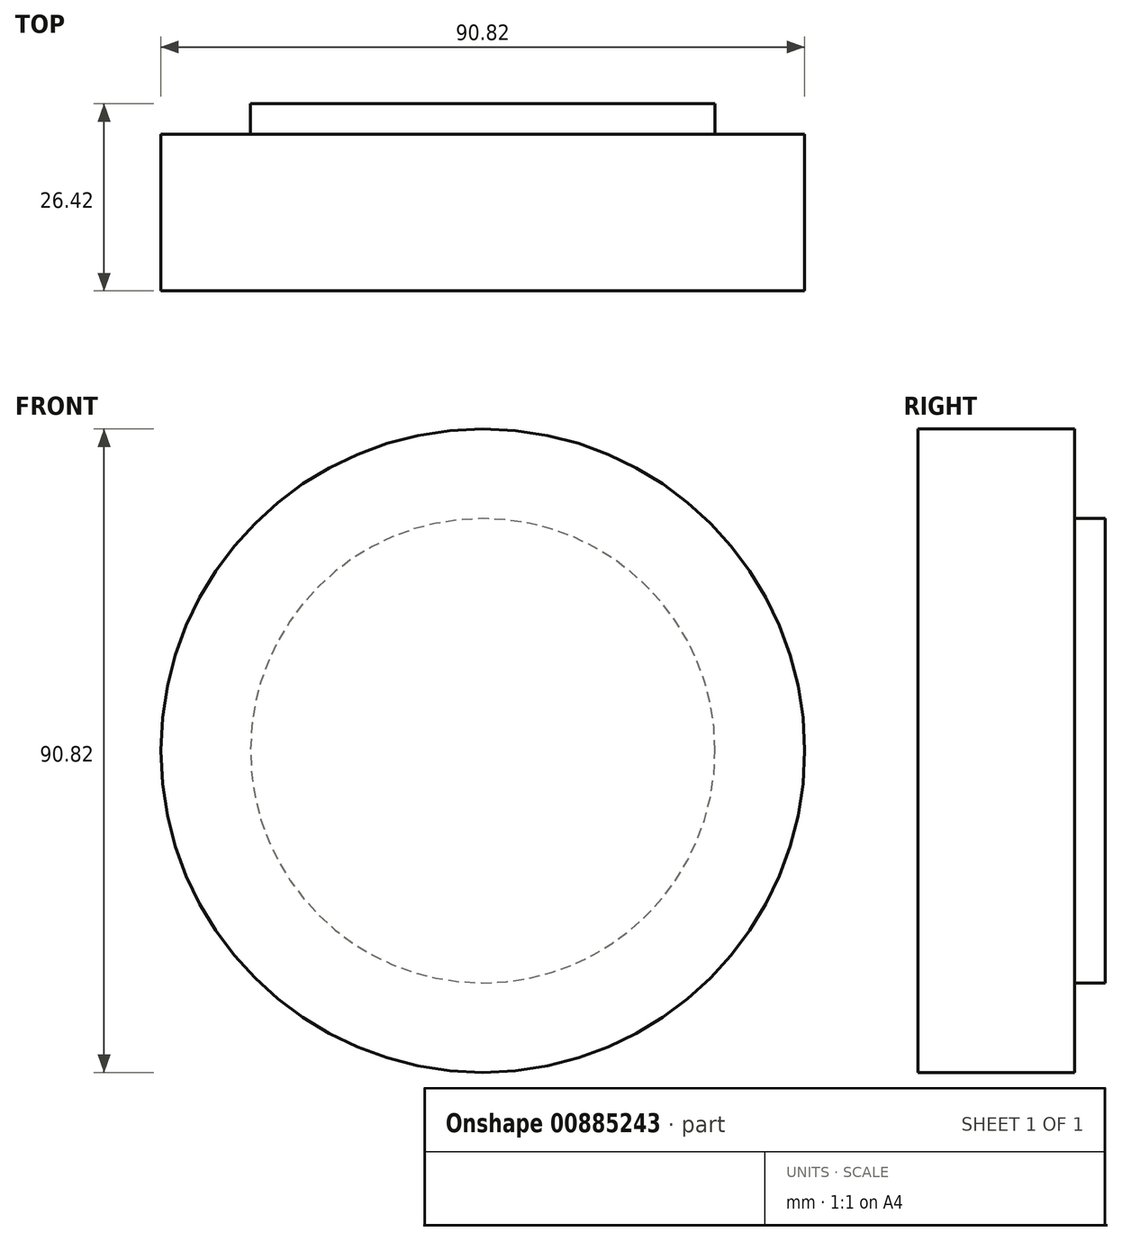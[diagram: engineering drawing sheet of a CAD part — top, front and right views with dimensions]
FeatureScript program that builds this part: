
annotation { "Feature Type Name" : "Feature", "Feature Type Description" : "" }
export const myFeature = defineFeature(function(context is Context, id is Id, definition is map)
    precondition{}
    {
        {
            var Q0;
            Q0=qCreatedBy(makeId("Front.planeOp"),FACE);
            var sketch = newSketch(context, id + "F0", { "sketchPlane" : qUnion([Q0])});
            skCircle(sketch, "E0", {"center": v(0, 0) * mm, "radius": 45.41 * mm});
            skCircle(sketch, "E1", {"center": v(0, 0) * mm, "radius": 32.77 * mm});
            skSolve(sketch);
        }
        {
            var Q0;
            Q0=makeQuery(id+"F0.imprint","IMPRINT",FACE,{"disambiguationData":[TD([[makeQuery(id+"F0.imprint","IMPRINT",EDGE,{"derivedFrom":sQuery(id+"F0.wireOp",EDGE,"E1")}),1.0]])]});
            extrude(context, id + "F1", {"entities" : qUnion([Q0]), "oppositeDirection" : true, "depth" : 4.32 * mm, "offsetDistance" : 25.4 * mm});
        }
        {
            var Q0;
            Q0 = qSketchRegion(id + "F0", true);
            var Q1;
            Q1=makeQuery(id+"F1.opExtrude","CAP_FACE",FACE,{"disambiguationData":[OSD([sQuery(id+"F0.wireOp",EDGE,"E1")])],"isStart":false});
            var Q2;
            Q2=makeQuery(id+"F1.opExtrude","CAP_FACE",FACE,{"disambiguationData":[OSD([sQuery(id+"F0.wireOp",EDGE,"E1")])],"isStart":true});
            extrude(context, id + "F2", {"entities" : qUnion([Q0, Q1, Q2]), "operationType" : NewBodyOperationType.ADD, "oppositeDirection" : true, "depth" : 22.1 * mm, "offsetDistance" : 25.4 * mm});
        }
    });
